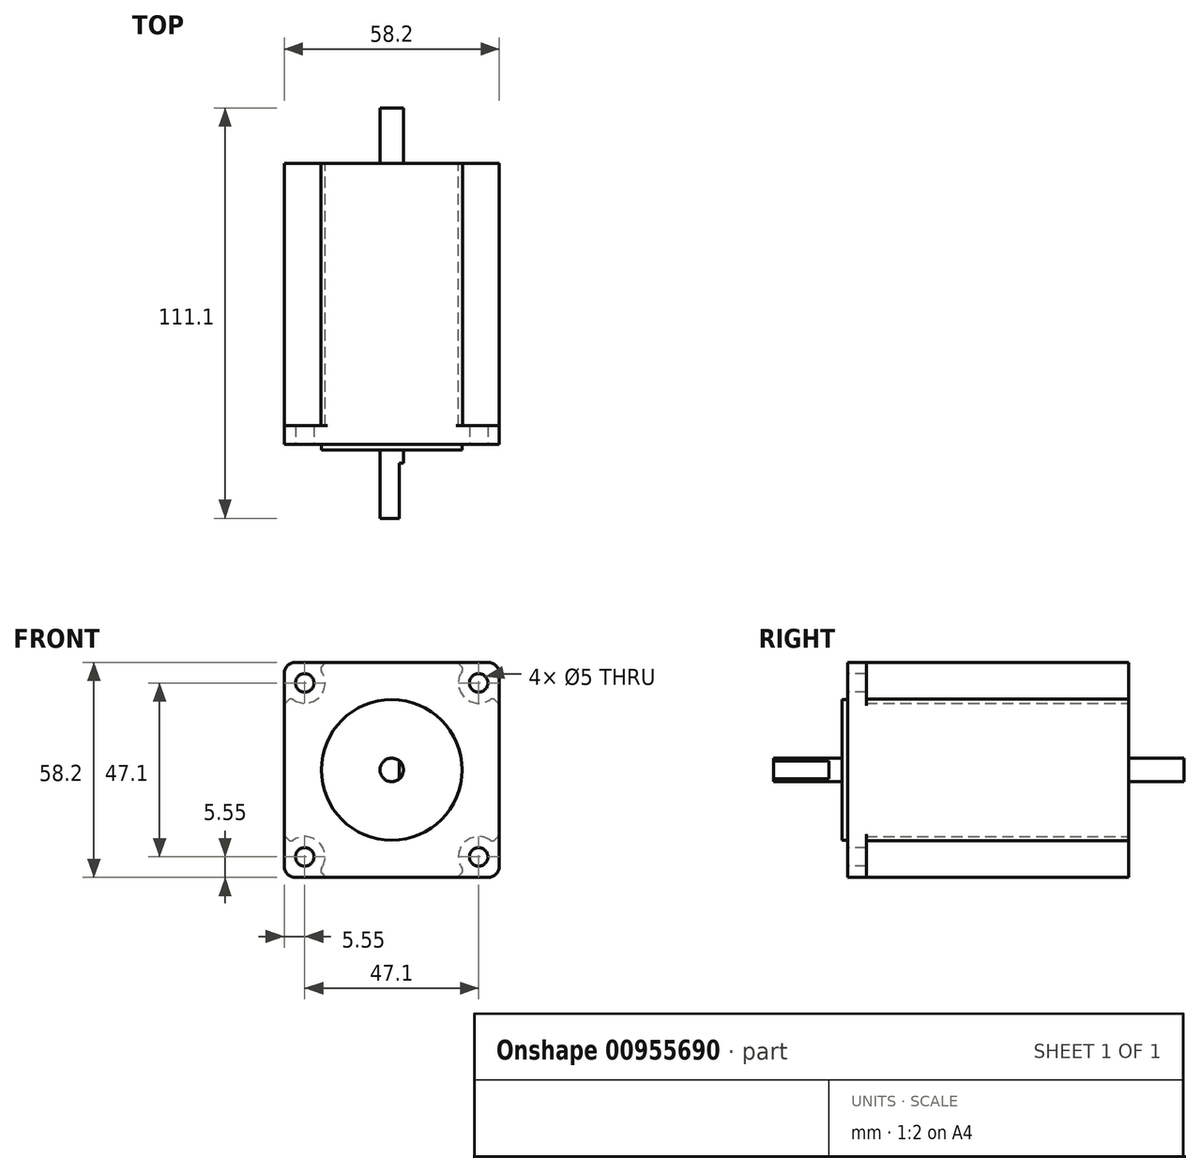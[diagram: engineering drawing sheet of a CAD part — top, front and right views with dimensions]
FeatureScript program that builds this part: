
annotation { "Feature Type Name" : "Feature", "Feature Type Description" : "" }
export const myFeature = defineFeature(function(context is Context, id is Id, definition is map)
    precondition{}
    {
        {
            var Q0;
            Q0=qCreatedBy(makeId("Front.planeOp"),FACE);
            var sketch = newSketch(context, id + "F0", { "sketchPlane" : qUnion([Q0])});
            skLineSegment(sketch, "E0.bottom", {"start": v(-29.1, 29.1) * mm, "end": v(29.1, 29.1) * mm});
            skLineSegment(sketch, "E0.top", {"start": v(-29.1, -29.1) * mm, "end": v(29.1, -29.1) * mm});
            skLineSegment(sketch, "E0.left", {"start": v(-29.1, 29.1) * mm, "end": v(-29.1, -29.1) * mm});
            skLineSegment(sketch, "E0.right", {"start": v(29.1, 29.1) * mm, "end": v(29.1, -29.1) * mm});
            skSolve(sketch);
        }
        {
            var Q0;
            Q0=makeQuery(id+"F0.imprint","IMPRINT",FACE,{"disambiguationData":[TD([[makeQuery(id+"F0.imprint","IMPRINT",EDGE,{"derivedFrom":sQuery(id+"F0.wireOp",EDGE,"E0.bottom")}),-1.0]])]});
            extrude(context, id + "F1", {"entities" : qUnion([Q0]), "depth" : 76 * mm, "offsetDistance" : 25 * mm});
        }
        {
            var Q0;
            Q0=makeQuery(id+"F1.opExtrude","CAP_FACE",FACE,{"disambiguationData":[OSD([sQuery(id+"F0.wireOp",EDGE,"E0.bottom"),sQuery(id+"F0.wireOp",EDGE,"E0.top"),sQuery(id+"F0.wireOp",EDGE,"E0.left"),sQuery(id+"F0.wireOp",EDGE,"E0.right")])],"isStart":false});
            var sketch = newSketch(context, id + "F2", { "sketchPlane" : qUnion([Q0])});
            skCircle(sketch, "E1", {"center": v(23.55, 23.55) * mm, "radius": 2.5 * mm});
            skCircle(sketch, "E2", {"center": v(23.55, -23.55) * mm, "radius": 2.5 * mm});
            skCircle(sketch, "E3", {"center": v(-23.55, -23.55) * mm, "radius": 2.5 * mm});
            skCircle(sketch, "E4", {"center": v(-23.55, 23.55) * mm, "radius": 2.5 * mm});
            skSolve(sketch);
        }
        {
            var Q0;
            Q0=qSketchRegion(id+"F2",true);
            extrude(context, id + "F3", {"entities" : qUnion([Q0]), "operationType" : NewBodyOperationType.REMOVE, "oppositeDirection" : true, "depth" : 25 * mm, "offsetDistance" : 25 * mm});
        }
        {
            var Q0;
            Q0=makeQuery(id+"F1.opExtrude","CAP_FACE",FACE,{"disambiguationData":[OSD([sQuery(id+"F0.wireOp",EDGE,"E0.bottom"),sQuery(id+"F0.wireOp",EDGE,"E0.top"),sQuery(id+"F0.wireOp",EDGE,"E0.left"),sQuery(id+"F0.wireOp",EDGE,"E0.right")])],"isStart":true});
            var sketch = newSketch(context, id + "F4", { "sketchPlane" : qUnion([Q0])});
            skLineSegment(sketch, "E5", {"start": v(46.89, 0) * mm, "end": v(27.33, 19.56) * mm});
            skArc(sketch, "E6", {"start": v(19.56, 27.33) * mm, "mid": v(19.66, 19.66) * mm, "end": v(27.33, 19.56) * mm});
            skLineSegment(sketch, "E7.trimOffspring", {"start": v(19.56, 27.33) * mm, "end": v(0, 46.89) * mm});
            skLineSegment(sketch, "E8.MirrorCS", {"start": v(46.89, 0) * mm, "end": v(27.33, -19.56) * mm});
            skArc(sketch, "E9.MirrorCS", {"start": v(19.56, -27.33) * mm, "mid": v(19.66, -19.66) * mm, "end": v(27.33, -19.56) * mm});
            skLineSegment(sketch, "E10.MirrorCS", {"start": v(19.56, -27.33) * mm, "end": v(0, -46.89) * mm});
            skLineSegment(sketch, "E11.MirrorCS", {"start": v(-19.56, -27.33) * mm, "end": v(0, -46.89) * mm});
            skArc(sketch, "E12.MirrorCS", {"start": v(-19.56, -27.33) * mm, "mid": v(-19.66, -19.66) * mm, "end": v(-27.33, -19.56) * mm});
            skLineSegment(sketch, "E13.MirrorCS", {"start": v(-46.89, 0) * mm, "end": v(-27.33, -19.56) * mm});
            skLineSegment(sketch, "E14.MirrorCS", {"start": v(-46.89, 0) * mm, "end": v(-27.33, 19.56) * mm});
            skArc(sketch, "E15.MirrorCS", {"start": v(-19.56, 27.33) * mm, "mid": v(-19.66, 19.66) * mm, "end": v(-27.33, 19.56) * mm});
            skLineSegment(sketch, "E16.MirrorCS", {"start": v(-19.56, 27.33) * mm, "end": v(0, 46.89) * mm});
            skLineSegment(sketch, "E17.bottom", {"start": v(76.66, -75.72) * mm, "end": v(-78.32, -75.72) * mm});
            skLineSegment(sketch, "E17.top", {"start": v(76.66, 78.3) * mm, "end": v(-78.32, 78.3) * mm});
            skLineSegment(sketch, "E17.left", {"start": v(76.66, -75.72) * mm, "end": v(76.66, 78.3) * mm});
            skLineSegment(sketch, "E17.right", {"start": v(-78.32, -75.72) * mm, "end": v(-78.32, 78.3) * mm});
            skSolve(sketch);
        }
        {
            var Q0;
            Q0=qSketchRegion(id+"F4",true);
            extrude(context, id + "F5", {"entities" : qUnion([Q0]), "operationType" : NewBodyOperationType.REMOVE, "oppositeDirection" : true, "depth" : 71 * mm, "offsetDistance" : 25 * mm});
        }
        {
            var Q0;
            Q0=makeQuery(id+"F5.boolean.opBoolean","INTERSECT",EDGE,{"derivedFrom":[makeQuery(id+"F1.opExtrude","SWEPT_FACE",FACE,{"disambiguationData":[OSD([sQuery(id+"F0.wireOp",EDGE,"E0.left")])]}),makeQuery(id+"F5.opExtrude","SWEPT_FACE",FACE,{"disambiguationData":[OSD([sQuery(id+"F4.wireOp",EDGE,"E5")])]})]});
            var Q1;
            Q1=makeQuery(id+"F5.boolean.opBoolean","INTERSECT",EDGE,{"derivedFrom":[makeQuery(id+"F1.opExtrude","SWEPT_FACE",FACE,{"disambiguationData":[OSD([sQuery(id+"F0.wireOp",EDGE,"E0.bottom")])]}),makeQuery(id+"F5.opExtrude","SWEPT_FACE",FACE,{"disambiguationData":[OSD([sQuery(id+"F4.wireOp",EDGE,"E7.trimOffspring")])]})]});
            var Q2;
            Q2=makeQuery(id+"F5.boolean.opBoolean","COPY",EDGE,{"derivedFrom":makeQuery(id+"F5.opExtrude","SWEPT_EDGE",EDGE,{"disambiguationData":[OSD([sQuery(id+"F4.wireOp",EDGE,"E6"),sQuery(id+"F4.wireOp",EDGE,"E7.trimOffspring")])]})});
            var Q3;
            Q3=makeQuery(id+"F5.boolean.opBoolean","COPY",EDGE,{"derivedFrom":makeQuery(id+"F5.opExtrude","SWEPT_EDGE",EDGE,{"disambiguationData":[OSD([sQuery(id+"F4.wireOp",EDGE,"E5"),sQuery(id+"F4.wireOp",EDGE,"E6")])]})});
            var Q4;
            Q4=makeQuery(id+"F5.boolean.opBoolean","INTERSECT",EDGE,{"derivedFrom":[makeQuery(id+"F1.opExtrude","SWEPT_FACE",FACE,{"disambiguationData":[OSD([sQuery(id+"F0.wireOp",EDGE,"E0.left")])]}),makeQuery(id+"F5.opExtrude","SWEPT_FACE",FACE,{"disambiguationData":[OSD([sQuery(id+"F4.wireOp",EDGE,"E8.MirrorCS")])]})]});
            var Q5;
            Q5=makeQuery(id+"F5.boolean.opBoolean","COPY",EDGE,{"derivedFrom":makeQuery(id+"F5.opExtrude","SWEPT_EDGE",EDGE,{"disambiguationData":[OSD([sQuery(id+"F4.wireOp",EDGE,"E8.MirrorCS"),sQuery(id+"F4.wireOp",EDGE,"E9.MirrorCS")])]})});
            var Q6;
            Q6=makeQuery(id+"F5.boolean.opBoolean","INTERSECT",EDGE,{"derivedFrom":[makeQuery(id+"F1.opExtrude","SWEPT_FACE",FACE,{"disambiguationData":[OSD([sQuery(id+"F0.wireOp",EDGE,"E0.top")])]}),makeQuery(id+"F5.opExtrude","SWEPT_FACE",FACE,{"disambiguationData":[OSD([sQuery(id+"F4.wireOp",EDGE,"E10.MirrorCS")])]})]});
            var Q7;
            Q7=makeQuery(id+"F5.boolean.opBoolean","COPY",EDGE,{"derivedFrom":makeQuery(id+"F5.opExtrude","SWEPT_EDGE",EDGE,{"disambiguationData":[OSD([sQuery(id+"F4.wireOp",EDGE,"E9.MirrorCS"),sQuery(id+"F4.wireOp",EDGE,"E10.MirrorCS")])]})});
            var Q8;
            Q8=makeQuery(id+"F5.boolean.opBoolean","INTERSECT",EDGE,{"derivedFrom":[makeQuery(id+"F1.opExtrude","SWEPT_FACE",FACE,{"disambiguationData":[OSD([sQuery(id+"F0.wireOp",EDGE,"E0.top")])]}),makeQuery(id+"F5.opExtrude","SWEPT_FACE",FACE,{"disambiguationData":[OSD([sQuery(id+"F4.wireOp",EDGE,"E11.MirrorCS")])]})]});
            var Q9;
            Q9=makeQuery(id+"F5.boolean.opBoolean","COPY",EDGE,{"derivedFrom":makeQuery(id+"F5.opExtrude","SWEPT_EDGE",EDGE,{"disambiguationData":[OSD([sQuery(id+"F4.wireOp",EDGE,"E11.MirrorCS"),sQuery(id+"F4.wireOp",EDGE,"E12.MirrorCS")])]})});
            var Q10;
            Q10=makeQuery(id+"F5.boolean.opBoolean","COPY",EDGE,{"derivedFrom":makeQuery(id+"F5.opExtrude","SWEPT_EDGE",EDGE,{"disambiguationData":[OSD([sQuery(id+"F4.wireOp",EDGE,"E12.MirrorCS"),sQuery(id+"F4.wireOp",EDGE,"E13.MirrorCS")])]})});
            var Q11;
            Q11=makeQuery(id+"F5.boolean.opBoolean","INTERSECT",EDGE,{"derivedFrom":[makeQuery(id+"F1.opExtrude","SWEPT_FACE",FACE,{"disambiguationData":[OSD([sQuery(id+"F0.wireOp",EDGE,"E0.right")])]}),makeQuery(id+"F5.opExtrude","SWEPT_FACE",FACE,{"disambiguationData":[OSD([sQuery(id+"F4.wireOp",EDGE,"E13.MirrorCS")])]})]});
            var Q12;
            Q12=makeQuery(id+"F5.boolean.opBoolean","COPY",EDGE,{"derivedFrom":makeQuery(id+"F5.opExtrude","SWEPT_EDGE",EDGE,{"disambiguationData":[OSD([sQuery(id+"F4.wireOp",EDGE,"E14.MirrorCS"),sQuery(id+"F4.wireOp",EDGE,"E15.MirrorCS")])]})});
            var Q13;
            Q13=makeQuery(id+"F5.boolean.opBoolean","INTERSECT",EDGE,{"derivedFrom":[makeQuery(id+"F1.opExtrude","SWEPT_FACE",FACE,{"disambiguationData":[OSD([sQuery(id+"F0.wireOp",EDGE,"E0.right")])]}),makeQuery(id+"F5.opExtrude","SWEPT_FACE",FACE,{"disambiguationData":[OSD([sQuery(id+"F4.wireOp",EDGE,"E14.MirrorCS")])]})]});
            var Q14;
            Q14=makeQuery(id+"F5.boolean.opBoolean","COPY",EDGE,{"derivedFrom":makeQuery(id+"F5.opExtrude","SWEPT_EDGE",EDGE,{"disambiguationData":[OSD([sQuery(id+"F4.wireOp",EDGE,"E15.MirrorCS"),sQuery(id+"F4.wireOp",EDGE,"E16.MirrorCS")])]})});
            var Q15;
            Q15=makeQuery(id+"F5.boolean.opBoolean","INTERSECT",EDGE,{"derivedFrom":[makeQuery(id+"F1.opExtrude","SWEPT_FACE",FACE,{"disambiguationData":[OSD([sQuery(id+"F0.wireOp",EDGE,"E0.bottom")])]}),makeQuery(id+"F5.opExtrude","SWEPT_FACE",FACE,{"disambiguationData":[OSD([sQuery(id+"F4.wireOp",EDGE,"E16.MirrorCS")])]})]});
            fillet(context, id + "F6", {"entities" : qUnion([Q0, Q1, Q2, Q3, Q4, Q5, Q6, Q7, Q8, Q9, Q10, Q11, Q12, Q13, Q14, Q15]), "radius" : 1 * mm, "tangentPropagation" : true, "allowEdgeOverflow" : false});
        }
        {
            var Q0;
            Q0=makeQuery(id+"F1.opExtrude","SWEPT_EDGE",EDGE,{"disambiguationData":[OSD([sQuery(id+"F0.wireOp",EDGE,"E0.top"),sQuery(id+"F0.wireOp",EDGE,"E0.left")])]});
            var Q1;
            Q1=makeQuery(id+"F1.opExtrude","SWEPT_EDGE",EDGE,{"disambiguationData":[OSD([sQuery(id+"F0.wireOp",EDGE,"E0.bottom"),sQuery(id+"F0.wireOp",EDGE,"E0.left")])]});
            var Q2;
            Q2=makeQuery(id+"F1.opExtrude","SWEPT_EDGE",EDGE,{"disambiguationData":[OSD([sQuery(id+"F0.wireOp",EDGE,"E0.top"),sQuery(id+"F0.wireOp",EDGE,"E0.right")])]});
            var Q3;
            Q3=makeQuery(id+"F1.opExtrude","SWEPT_EDGE",EDGE,{"disambiguationData":[OSD([sQuery(id+"F0.wireOp",EDGE,"E0.bottom"),sQuery(id+"F0.wireOp",EDGE,"E0.right")])]});
            fillet(context, id + "F7", {"entities" : qUnion([Q0, Q1, Q2, Q3]), "radius" : 3 * mm, "tangentPropagation" : true, "allowEdgeOverflow" : false});
        }
        {
            var Q0;
            Q0=makeQuery(id+"F1.opExtrude","CAP_FACE",FACE,{"disambiguationData":[OSD([sQuery(id+"F0.wireOp",EDGE,"E0.bottom"),sQuery(id+"F0.wireOp",EDGE,"E0.top"),sQuery(id+"F0.wireOp",EDGE,"E0.left"),sQuery(id+"F0.wireOp",EDGE,"E0.right")])],"isStart":false});
            var sketch = newSketch(context, id + "F8", { "sketchPlane" : qUnion([Q0])});
            skCircle(sketch, "E18", {"center": v(0, 0) * mm, "radius": 19.05 * mm});
            skSolve(sketch);
        }
        {
            var Q0;
            Q0=makeQuery(id+"F8.imprint","IMPRINT",FACE,{"disambiguationData":[TD([[makeQuery(id+"F8.imprint","IMPRINT",EDGE,{"derivedFrom":sQuery(id+"F8.wireOp",EDGE,"E18")}),1.0]])]});
            extrude(context, id + "F9", {"entities" : qUnion([Q0]), "operationType" : NewBodyOperationType.ADD, "depth" : 1.6 * mm, "offsetDistance" : 25 * mm});
        }
        {
            var Q0;
            Q0=makeQuery(id+"F9.opExtrude","CAP_FACE",FACE,{"disambiguationData":[OSD([sQuery(id+"F8.wireOp",EDGE,"E18")])],"isStart":false});
            var sketch = newSketch(context, id + "F10", { "sketchPlane" : qUnion([Q0])});
            skCircle(sketch, "E19", {"center": v(0, 0) * mm, "radius": 3.17 * mm});
            skSolve(sketch);
        }
        {
            var Q0;
            Q0=makeQuery(id+"F10.imprint","IMPRINT",FACE,{"disambiguationData":[TD([[makeQuery(id+"F10.imprint","IMPRINT",EDGE,{"derivedFrom":sQuery(id+"F10.wireOp",EDGE,"E19")}),1.0]])]});
            var Q1;
            Q1=sQuery(id+"F10.wireOp",EDGE,"E19");
            extrude(context, id + "F11", {"entities" : qUnion([Q0]), "operationType" : NewBodyOperationType.ADD, "surfaceEntities" : qUnion([Q1]), "depth" : (20.1 - 1.6) * mm, "offsetDistance" : 25 * mm});
        }
        {
            var Q0;
            Q0=makeQuery(id+"F11.opExtrude","CAP_FACE",FACE,{"disambiguationData":[OSD([sQuery(id+"F10.wireOp",EDGE,"E19")])],"isStart":false});
            var sketch = newSketch(context, id + "F12", { "sketchPlane" : qUnion([Q0])});
            skLineSegment(sketch, "E20.bottom", {"start": v(7, 5) * mm, "end": v(2, 5) * mm});
            skLineSegment(sketch, "E20.top", {"start": v(7, -5) * mm, "end": v(2, -5) * mm});
            skLineSegment(sketch, "E20.left", {"start": v(7, 5) * mm, "end": v(7, -5) * mm});
            skLineSegment(sketch, "E20.right", {"start": v(2, 5) * mm, "end": v(2, -5) * mm});
            skSolve(sketch);
        }
        {
            var Q0;
            {var subQ0=sQuery(id+"F12.wireOp",EDGE,"E20.right");var subQ1=makeQuery(id+"F11.opExtrude","CAP_EDGE",EDGE,{"disambiguationData":[OSD([sQuery(id+"F10.wireOp",EDGE,"E19")])],"isStart":false});var subQ2=makeQuery(id+"F12.imprint","INTERSECT",VERTEX,{"disambiguationData":[OD(0.0)],"derivedFrom":[subQ1,subQ0]});Q0=makeQuery(id+"F12.imprint","IMPRINT",FACE,{"disambiguationData":[TD([[makeQuery(id+"F12.imprint","IMPRINT",EDGE,{"disambiguationData":[TD([[subQ2,-1.0]])],"derivedFrom":subQ0}),1.0]])]});}
            var Q1;
            Q1=sQuery(id+"F12.wireOp",EDGE,"E20.bottom");
            var Q2;
            Q2=sQuery(id+"F12.wireOp",EDGE,"E20.right");
            var Q3;
            Q3=sQuery(id+"F12.wireOp",EDGE,"E20.top");
            var Q4;
            Q4=sQuery(id+"F12.wireOp",EDGE,"E20.left");
            extrude(context, id + "F13", {"entities" : qUnion([Q0]), "operationType" : NewBodyOperationType.REMOVE, "surfaceEntities" : qUnion([Q1, Q2, Q3, Q4]), "oppositeDirection" : true, "depth" : 15 * mm, "offsetDistance" : 25 * mm});
        }
        {
            var Q0;
            Q0=makeQuery(id+"F1.opExtrude","CAP_FACE",FACE,{"disambiguationData":[OSD([sQuery(id+"F0.wireOp",EDGE,"E0.bottom"),sQuery(id+"F0.wireOp",EDGE,"E0.top"),sQuery(id+"F0.wireOp",EDGE,"E0.left"),sQuery(id+"F0.wireOp",EDGE,"E0.right")])],"isStart":true});
            var sketch = newSketch(context, id + "F14", { "sketchPlane" : qUnion([Q0])});
            skCircle(sketch, "E21", {"center": v(0, 0) * mm, "radius": 3.17 * mm});
            skSolve(sketch);
        }
        {
            var Q0;
            Q0=makeQuery(id+"F14.imprint","IMPRINT",FACE,{"disambiguationData":[TD([[makeQuery(id+"F14.imprint","IMPRINT",EDGE,{"derivedFrom":sQuery(id+"F14.wireOp",EDGE,"E21")}),1.0]])]});
            extrude(context, id + "F15", {"entities" : qUnion([Q0]), "operationType" : NewBodyOperationType.ADD, "depth" : 15 * mm, "offsetDistance" : 25 * mm});
        }
    });
